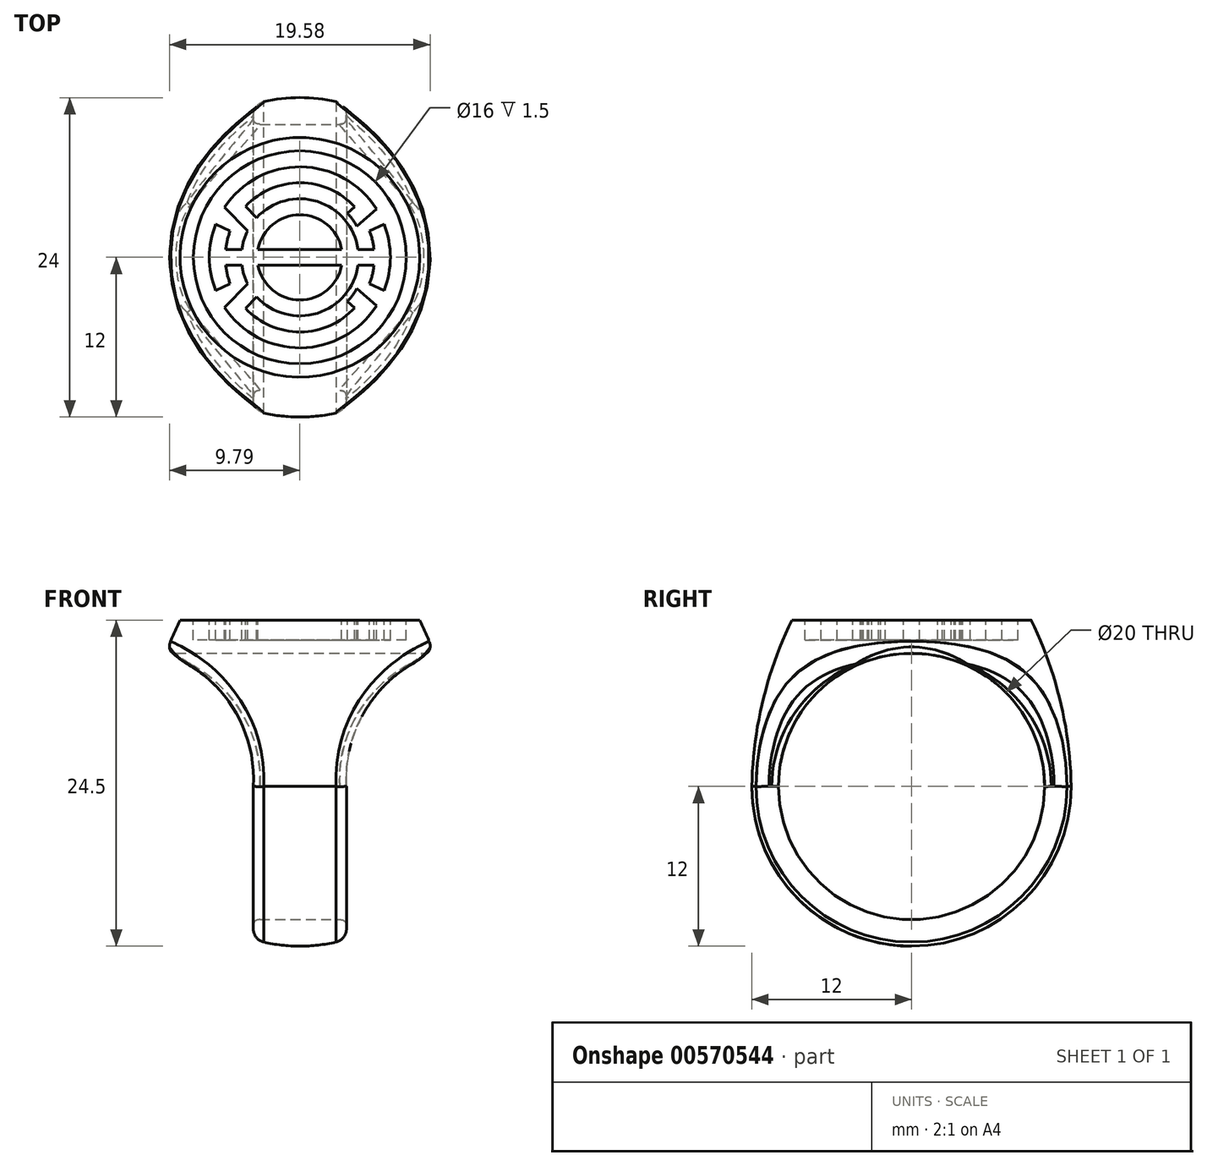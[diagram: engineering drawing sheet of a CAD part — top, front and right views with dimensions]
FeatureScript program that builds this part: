
annotation { "Feature Type Name" : "Feature", "Feature Type Description" : "" }
export const myFeature = defineFeature(function(context is Context, id is Id, definition is map)
    precondition{}
    {
        {
            var Q0;
            Q0=qCreatedBy(makeId("Right.planeOp"),FACE);
            var sketch = newSketch(context, id + "F0", { "sketchPlane" : qUnion([Q0])});
            skLineSegment(sketch, "E0", {"start": v(0, 0) * mm, "end": v(0, -24.5) * mm});
            skLineSegment(sketch, "E1", {"start": v(0, 0) * mm, "end": v(-9, 0) * mm});
            skArc(sketch, "E2", {"start": v(-12, -12.5) * mm, "mid": v(-8.49, -20.99) * mm, "end": v(0, -24.5) * mm});
            skLineSegment(sketch, "E3", {"start": v(0, -12.5) * mm, "end": v(-12, -12.5) * mm, "construction": true});
            skArc(sketch, "E4", {"start": v(-9, 0) * mm, "mid": v(-11.18, -6.09) * mm, "end": v(-12, -12.5) * mm});
            skSolve(sketch);
        }
        {
            var Q0;
            Q0=makeQuery(id+"F0.imprint","IMPRINT",FACE,{"disambiguationData":[TD([[makeQuery(id+"F0.imprint","IMPRINT",EDGE,{"derivedFrom":sQuery(id+"F0.wireOp",EDGE,"E0")}),-1.0]])]});
            var Q1;
            Q1=sQuery(id+"F0.wireOp",EDGE,"E0");
            revolve(context, id + "F1", {"entities" : qUnion([Q0]), "axis" : qUnion([Q1]), "revolveType" : RevolveType.FULL});
        }
        {
            var Q0;
            Q0=qCreatedBy(makeId("Right.planeOp"),FACE);
            var sketch = newSketch(context, id + "F2", { "sketchPlane" : qUnion([Q0])});
            skCircle(sketch, "E5", {"center": v(0, -12.5) * mm, "radius": 10 * mm});
            skSolve(sketch);
        }
        {
            var Q0;
            Q0 = qSketchRegion(id + "F2", true);
            extrude(context, id + "F3", {"entities" : qUnion([Q0]), "operationType" : NewBodyOperationType.REMOVE, "oppositeDirection" : true, "depth" : 25 * mm, "offsetDistance" : 25 * mm, "symmetric" : true});
        }
        {
            var Q0;
            Q0=qCreatedBy(makeId("Front.planeOp"),FACE);
            var sketch = newSketch(context, id + "F4", { "sketchPlane" : qUnion([Q0])});
            skLineSegment(sketch, "E6", {"start": v(3.5, -26.5) * mm, "end": v(3.5, -12.5) * mm});
            skArc(sketch, "E7", {"start": v(10.15, -2.5) * mm, "mid": v(5.16, -6.39) * mm, "end": v(3.5, -12.5) * mm});
            skLineSegment(sketch, "E8", {"start": v(10.15, -2.5) * mm, "end": v(11.65, -2.5) * mm});
            skLineSegment(sketch, "E9", {"start": v(11.65, -2.5) * mm, "end": v(11.65, -26.5) * mm});
            skLineSegment(sketch, "E10", {"start": v(11.65, -26.5) * mm, "end": v(3.5, -26.5) * mm});
            skPoint(sketch, "E11.start.orphan", {"position": v(0, -24.5) * mm});
            skLineSegment(sketch, "E12", {"start": v(0, 0) * mm, "end": v(0, -24.5) * mm, "construction": true});
            skLineSegment(sketch, "E13.MirrorCS", {"start": v(-3.5, -26.5) * mm, "end": v(-3.5, -12.5) * mm});
            skArc(sketch, "E14.MirrorCS", {"start": v(-10.15, -2.5) * mm, "mid": v(-5.16, -6.39) * mm, "end": v(-3.5, -12.5) * mm});
            skLineSegment(sketch, "E15.MirrorCS", {"start": v(-11.65, -2.5) * mm, "end": v(-11.65, -26.5) * mm});
            skLineSegment(sketch, "E16.MirrorCS", {"start": v(-11.65, -26.5) * mm, "end": v(-3.5, -26.5) * mm});
            skLineSegment(sketch, "E17.MirrorCS", {"start": v(-10.15, -2.5) * mm, "end": v(-11.65, -2.5) * mm});
            skSolve(sketch);
        }
        {
            var Q0;
            Q0 = qSketchRegion(id + "F4", true);
            extrude(context, id + "F5", {"entities" : qUnion([Q0]), "operationType" : NewBodyOperationType.REMOVE, "depth" : 25 * mm, "offsetDistance" : 25 * mm, "symmetric" : true});
        }
        {
            var Q0;
            Q0=makeQuery(id+"F1.opRevolve","SWEPT_FACE",FACE,{"disambiguationData":[OSD([sQuery(id+"F0.wireOp",EDGE,"E1")])]});
            var sketch = newSketch(context, id + "F6", { "sketchPlane" : qUnion([Q0])});
            skCircle(sketch, "E18", {"center": v(0, 0) * mm, "radius": 8 * mm});
            skLineSegment(sketch, "E19", {"start": v(-8, 0) * mm, "end": v(8, 0) * mm, "construction": true});
            skArc(sketch, "E20", {"start": v(3.14, 0.6) * mm, "mid": v(0, 3.2) * mm, "end": v(-3.14, 0.6) * mm});
            skArc(sketch, "E21", {"start": v(4.36, 0.6) * mm, "mid": v(1.32, 4.2) * mm, "end": v(-3.24, 2.98) * mm});
            skArc(sketch, "E22", {"start": v(5.57, 0.6) * mm, "mid": v(5.45, 1.3) * mm, "end": v(5.24, 1.98) * mm});
            skArc(sketch, "E23", {"start": v(6.8, 0) * mm, "mid": v(6.68, 1.26) * mm, "end": v(6.33, 2.49) * mm});
            skLineSegment(sketch, "E24", {"start": v(-4.08, 3.84) * mm, "end": v(-3.24, 2.98) * mm});
            skLineSegment(sketch, "E25", {"start": v(-5.67, 3.75) * mm, "end": v(-3.93, 1.98) * mm});
            skLineSegment(sketch, "E26", {"start": v(-6.33, 2.49) * mm, "end": v(-5.24, 1.98) * mm});
            skArc(sketch, "E27.trimOffspring", {"start": v(-6.33, 2.49) * mm, "mid": v(-6.68, 1.26) * mm, "end": v(-6.8, 0) * mm});
            skArc(sketch, "E28.trimOffspring", {"start": v(-5.24, 1.98) * mm, "mid": v(-5.45, 1.3) * mm, "end": v(-5.57, 0.6) * mm});
            skArc(sketch, "E29.trimOffspring", {"start": v(-3.93, 1.98) * mm, "mid": v(-4.2, 1.3) * mm, "end": v(-4.36, 0.6) * mm});
            skLineSegment(sketch, "E30", {"start": v(-5.57, 0.6) * mm, "end": v(-4.36, 0.6) * mm});
            skLineSegment(sketch, "E31", {"start": v(5.24, 1.98) * mm, "end": v(6.33, 2.49) * mm});
            skLineSegment(sketch, "E32", {"start": v(5.75, 3.62) * mm, "end": v(4.29, 2.33) * mm});
            skLineSegment(sketch, "E33", {"start": v(3.58, 3.3) * mm, "end": v(4.13, 3.79) * mm});
            skLineSegment(sketch, "E34.trimOffspring", {"start": v(4.36, 0.6) * mm, "end": v(5.57, 0.6) * mm});
            skPoint(sketch, "E35.orphan", {"position": v(4.4, 0) * mm});
            skPoint(sketch, "E36.orphan", {"position": v(5.6, 0) * mm});
            skArc(sketch, "E37.trimOffspring", {"start": v(4.13, 3.79) * mm, "mid": v(0.04, 5.6) * mm, "end": v(-4.08, 3.84) * mm});
            skArc(sketch, "E38.trimOffspring", {"start": v(5.75, 3.62) * mm, "mid": v(0.08, 6.8) * mm, "end": v(-5.67, 3.75) * mm});
            skPoint(sketch, "E39.orphan", {"position": v(-5.6, 0) * mm});
            skPoint(sketch, "E40.orphan", {"position": v(-4.4, 0) * mm});
            skLineSegment(sketch, "E41.trimOffspring", {"start": v(-3.14, 0.6) * mm, "end": v(3.14, 0.6) * mm});
            skPoint(sketch, "E42.orphan", {"position": v(-3.2, 0) * mm});
            skArc(sketch, "E43", {"start": v(4.29, 2.33) * mm, "mid": v(3.97, 2.84) * mm, "end": v(3.58, 3.3) * mm});
            skArc(sketch, "E44.MirrorCS", {"start": v(-6.33, -2.49) * mm, "mid": v(-6.68, -1.26) * mm, "end": v(-6.8, 0) * mm});
            skLineSegment(sketch, "E45.MirrorCS", {"start": v(-6.33, -2.49) * mm, "end": v(-5.24, -1.98) * mm});
            skArc(sketch, "E46.MirrorCS", {"start": v(-5.24, -1.98) * mm, "mid": v(-5.45, -1.3) * mm, "end": v(-5.57, -0.6) * mm});
            skLineSegment(sketch, "E47.MirrorCS", {"start": v(-5.57, -0.6) * mm, "end": v(-4.36, -0.6) * mm});
            skArc(sketch, "E48.MirrorCS", {"start": v(-3.93, -1.98) * mm, "mid": v(-4.2, -1.3) * mm, "end": v(-4.36, -0.6) * mm});
            skLineSegment(sketch, "E49.MirrorCS", {"start": v(-5.67, -3.75) * mm, "end": v(-3.93, -1.98) * mm});
            skArc(sketch, "E50.MirrorCS", {"start": v(5.75, -3.62) * mm, "mid": v(0.08, -6.8) * mm, "end": v(-5.67, -3.75) * mm});
            skLineSegment(sketch, "E51.MirrorCS", {"start": v(5.75, -3.62) * mm, "end": v(4.29, -2.33) * mm});
            skArc(sketch, "E52.MirrorCS", {"start": v(4.29, -2.33) * mm, "mid": v(3.97, -2.84) * mm, "end": v(3.58, -3.3) * mm});
            skArc(sketch, "E53.MirrorCS", {"start": v(4.13, -3.79) * mm, "mid": v(0.04, -5.6) * mm, "end": v(-4.08, -3.84) * mm});
            skLineSegment(sketch, "E54.MirrorCS", {"start": v(-4.08, -3.84) * mm, "end": v(-3.24, -2.98) * mm});
            skArc(sketch, "E55.MirrorCS", {"start": v(4.36, -0.6) * mm, "mid": v(1.32, -4.2) * mm, "end": v(-3.24, -2.98) * mm});
            skLineSegment(sketch, "E56.MirrorCS", {"start": v(4.36, -0.6) * mm, "end": v(5.57, -0.6) * mm});
            skArc(sketch, "E57.MirrorCS", {"start": v(5.57, -0.6) * mm, "mid": v(5.45, -1.3) * mm, "end": v(5.24, -1.98) * mm});
            skLineSegment(sketch, "E58.MirrorCS", {"start": v(5.24, -1.98) * mm, "end": v(6.33, -2.49) * mm});
            skArc(sketch, "E59.MirrorCS", {"start": v(6.8, 0) * mm, "mid": v(6.68, -1.26) * mm, "end": v(6.33, -2.49) * mm});
            skLineSegment(sketch, "E60.MirrorCS", {"start": v(-3.14, -0.6) * mm, "end": v(3.14, -0.6) * mm});
            skArc(sketch, "E61.MirrorCS", {"start": v(3.14, -0.6) * mm, "mid": v(0, -3.2) * mm, "end": v(-3.14, -0.6) * mm});
            skLineSegment(sketch, "E62.MirrorCS", {"start": v(3.58, -3.3) * mm, "end": v(4.13, -3.79) * mm});
            skSolve(sketch);
        }
        {
            var Q0;
            Q0=makeQuery(id+"F6.imprint","IMPRINT",FACE,{"disambiguationData":[TD([[makeQuery(id+"F6.imprint","IMPRINT",EDGE,{"derivedFrom":sQuery(id+"F6.wireOp",EDGE,"E18")}),1.0]])]});
            var Q1;
            Q1=makeQuery(id+"F6.imprint","IMPRINT",FACE,{"disambiguationData":[TD([[makeQuery(id+"F6.imprint","IMPRINT",EDGE,{"derivedFrom":sQuery(id+"F6.wireOp",EDGE,"E20")}),1.0]])]});
            var Q2;
            Q2=makeQuery(id+"F6.imprint","IMPRINT",FACE,{"disambiguationData":[TD([[makeQuery(id+"F6.imprint","IMPRINT",EDGE,{"derivedFrom":sQuery(id+"F6.wireOp",EDGE,"E60.MirrorCS")}),-1.0]])]});
            extrude(context, id + "F7", {"entities" : qUnion([Q0, Q1, Q2]), "operationType" : NewBodyOperationType.REMOVE, "oppositeDirection" : true, "depth" : 1.5 * mm, "offsetDistance" : 25 * mm});
        }
        {
            var Q0;
            Q0=makeQuery(id+"F5.boolean.opBoolean","INTERSECT",EDGE,{"disambiguationData":[OD(1.0)],"derivedFrom":[makeQuery(id+"F1.opRevolve","SWEPT_FACE",FACE,{"disambiguationData":[OSD([sQuery(id+"F0.wireOp",EDGE,"E4")])]}),makeQuery(id+"F5.opExtrude","SWEPT_FACE",FACE,{"disambiguationData":[OSD([sQuery(id+"F4.wireOp",EDGE,"E14.MirrorCS")])]})]});
            var Q1;
            Q1=makeQuery(id+"F5.boolean.opBoolean","INTERSECT",EDGE,{"derivedFrom":[makeQuery(id+"F1.opRevolve","SWEPT_FACE",FACE,{"disambiguationData":[OSD([sQuery(id+"F0.wireOp",EDGE,"E2")])]}),makeQuery(id+"F5.opExtrude","SWEPT_FACE",FACE,{"disambiguationData":[OSD([sQuery(id+"F4.wireOp",EDGE,"E13.MirrorCS")])]})]});
            var Q2;
            Q2=makeQuery(id+"F5.boolean.opBoolean","INTERSECT",EDGE,{"disambiguationData":[OD(1.0)],"derivedFrom":[makeQuery(id+"F1.opRevolve","SWEPT_FACE",FACE,{"disambiguationData":[OSD([sQuery(id+"F0.wireOp",EDGE,"E4")])]}),makeQuery(id+"F5.opExtrude","SWEPT_FACE",FACE,{"disambiguationData":[OSD([sQuery(id+"F4.wireOp",EDGE,"E7")])]})]});
            var Q3;
            Q3=makeQuery(id+"F5.boolean.opBoolean","INTERSECT",EDGE,{"derivedFrom":[makeQuery(id+"F1.opRevolve","SWEPT_FACE",FACE,{"disambiguationData":[OSD([sQuery(id+"F0.wireOp",EDGE,"E2")])]}),makeQuery(id+"F5.opExtrude","SWEPT_FACE",FACE,{"disambiguationData":[OSD([sQuery(id+"F4.wireOp",EDGE,"E6")])]})]});
            fillet(context, id + "F8", {"entities" : qUnion([Q0, Q1, Q2, Q3]), "radius" : 1 * mm, "allowEdgeOverflow" : false});
        }
        {
            var Q0;
            Q0=makeQuery(id+"F5.boolean.opBoolean","INTERSECT",EDGE,{"disambiguationData":[OD(1.0)],"derivedFrom":[makeQuery(id+"F3.boolean.opBoolean","COPY",FACE,{"derivedFrom":makeQuery(id+"F3.opExtrude","SWEPT_FACE",FACE,{"disambiguationData":[OSD([sQuery(id+"F2.wireOp",EDGE,"E5")])]})}),makeQuery(id+"F5.opExtrude","SWEPT_FACE",FACE,{"disambiguationData":[OSD([sQuery(id+"F4.wireOp",EDGE,"E14.MirrorCS")])]})]});
            var Q1;
            Q1=makeQuery(id+"F5.boolean.opBoolean","INTERSECT",EDGE,{"derivedFrom":[makeQuery(id+"F3.boolean.opBoolean","COPY",FACE,{"derivedFrom":makeQuery(id+"F3.opExtrude","SWEPT_FACE",FACE,{"disambiguationData":[OSD([sQuery(id+"F2.wireOp",EDGE,"E5")])]})}),makeQuery(id+"F5.opExtrude","SWEPT_FACE",FACE,{"disambiguationData":[OSD([sQuery(id+"F4.wireOp",EDGE,"E13.MirrorCS")])]})]});
            var Q2;
            Q2=makeQuery(id+"F5.boolean.opBoolean","INTERSECT",EDGE,{"disambiguationData":[OD(0.0)],"derivedFrom":[makeQuery(id+"F3.boolean.opBoolean","COPY",FACE,{"derivedFrom":makeQuery(id+"F3.opExtrude","SWEPT_FACE",FACE,{"disambiguationData":[OSD([sQuery(id+"F2.wireOp",EDGE,"E5")])]})}),makeQuery(id+"F5.opExtrude","SWEPT_FACE",FACE,{"disambiguationData":[OSD([sQuery(id+"F4.wireOp",EDGE,"E14.MirrorCS")])]})]});
            var Q3;
            Q3=makeQuery(id+"F5.boolean.opBoolean","INTERSECT",EDGE,{"disambiguationData":[OD(0.0)],"derivedFrom":[makeQuery(id+"F3.boolean.opBoolean","COPY",FACE,{"derivedFrom":makeQuery(id+"F3.opExtrude","SWEPT_FACE",FACE,{"disambiguationData":[OSD([sQuery(id+"F2.wireOp",EDGE,"E5")])]})}),makeQuery(id+"F5.opExtrude","SWEPT_FACE",FACE,{"disambiguationData":[OSD([sQuery(id+"F4.wireOp",EDGE,"E7")])]})]});
            var Q4;
            Q4=makeQuery(id+"F3.boolean.opBoolean","COPY",FACE,{"derivedFrom":makeQuery(id+"F3.opExtrude","SWEPT_FACE",FACE,{"disambiguationData":[OSD([sQuery(id+"F2.wireOp",EDGE,"E5")])]})});
            fillet(context, id + "F9", {"entities" : qUnion([Q0, Q1, Q2, Q3, Q4]), "radius" : .5 * mm, "rho" : 0.5, "crossSection" : FilletCrossSection.CONIC, "allowEdgeOverflow" : false});
        }
    });
